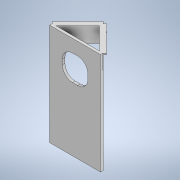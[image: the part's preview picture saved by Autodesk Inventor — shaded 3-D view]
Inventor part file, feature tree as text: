
AUTODESK INVENTOR PART (.ipt)
format: ipt  version: 2020 (Build 240168000, 168)  size: 164,352 bytes
history: native  units: mm
features: extrude x4, sketch x4
ambient origin geometry x8: Origin, YZ Plane, XZ Plane, XY Plane, X Axis, Y Axis, Z Axis, Center Point
bodies: Solid1 (feature_tree)
feature tree (8):
  extrude  "Extrusion1"  Depth=200.0mm
  extrude  "Extrusion2"  TaperAngle=45.0deg  [1 undecoded]
  extrude  "Extrusion6"  Depth=5.0mm
  extrude  "Extrusion9"  Depth=50.0mm
  sketch  "Sketch1"  dims[d0=100.0mm d1=200.0mm]
  sketch  "Sketch2"  dims[d2=5.0mm d3=0.0mm d4=45.0deg]
  sketch  "Sketch6"  dims[d5=5.0mm d6=5.0mm]
  sketch  "Sketch10"  dims[d7=30.0mm d8=0.0mm d21=50.0mm d22=50.0mm d23=20.0mm d24=5.0mm d25=0.0mm d33=5.0mm d34=5.0mm d36=3.0mm d37=0.0mm]
note: 1 required parameter value undecoded (feature->parameter linkage not recoverable at this tier; creation-order binding heuristic only, values carry confidence <= 0.55)
